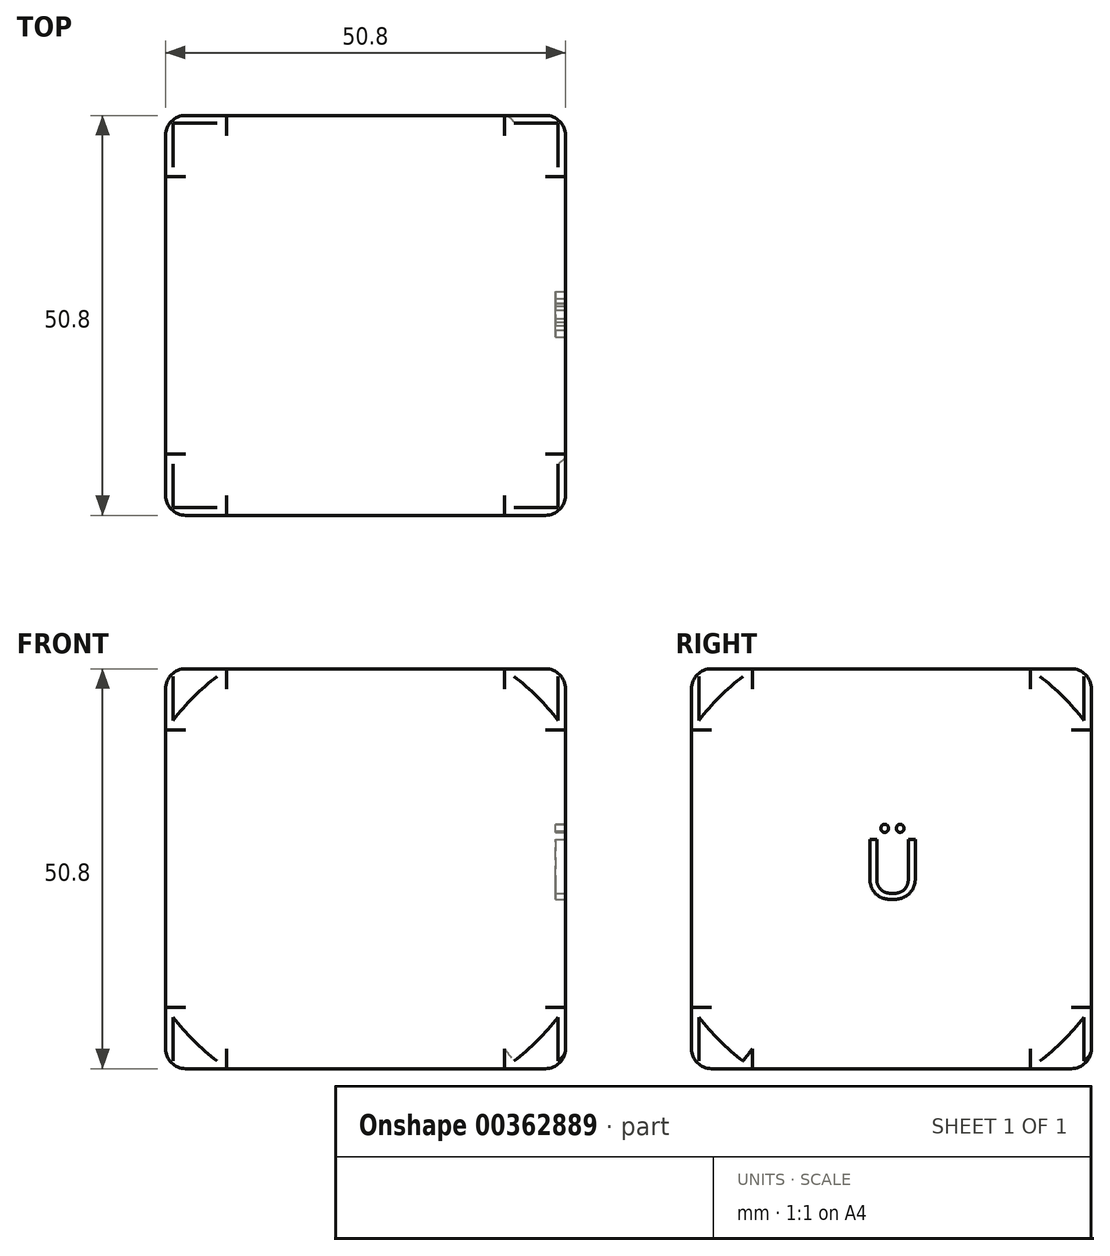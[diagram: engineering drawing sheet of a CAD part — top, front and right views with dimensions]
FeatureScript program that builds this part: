
annotation { "Feature Type Name" : "Feature", "Feature Type Description" : "" }
export const myFeature = defineFeature(function(context is Context, id is Id, definition is map)
    precondition{}
    {
        {
            var Q0;
            Q0=qCreatedBy(makeId("Front.planeOp"),FACE);
            var sketch = newSketch(context, id + "F0", { "sketchPlane" : qUnion([Q0])});
            skLineSegment(sketch, "E0.bottom", {"start": v(25.4, -25.4) * mm, "end": v(-25.4, -25.4) * mm});
            skLineSegment(sketch, "E0.top", {"start": v(25.4, 25.4) * mm, "end": v(-25.4, 25.4) * mm});
            skLineSegment(sketch, "E0.left", {"start": v(25.4, -25.4) * mm, "end": v(25.4, 25.4) * mm});
            skLineSegment(sketch, "E0.right", {"start": v(-25.4, -25.4) * mm, "end": v(-25.4, 25.4) * mm});
            skPoint(sketch, "E0.middle", {"position": v(0, 0) * mm});
            skSolve(sketch);
        }
        {
            var Q0;
            Q0 = qSketchRegion(id + "F0", true);
            extrude(context, id + "F1", {"entities" : qUnion([Q0]), "endBound" : BoundingType.SYMMETRIC, "oppositeDirection" : true, "depth" : 50.8 * mm});
        }
        {
            var Q0;
            Q0=qCreatedBy(makeId("Right.planeOp"),FACE);
            var sketch = newSketch(context, id + "F2", { "sketchPlane" : qUnion([Q0])});
            skArc(sketch, "E1", {"start": v(0, 39.37) * mm, "mid": v(-39.37, 0) * mm, "end": v(0, -39.37) * mm});
            skLineSegment(sketch, "E2", {"start": v(0, -76.2) * mm, "end": v(0, -39.37) * mm});
            skArc(sketch, "E3", {"start": v(0, 76.2) * mm, "mid": v(-76.2, 0) * mm, "end": v(0, -76.2) * mm});
            skPoint(sketch, "E4.orphan", {"position": v(0, 68.2) * mm});
            skLineSegment(sketch, "E5.trimOffspring", {"start": v(0, 39.37) * mm, "end": v(0, 76.2) * mm});
            skSolve(sketch);
        }
        {
            var Q0;
            Q0 = qSketchRegion(id + "F2", true);
            var Q1;
            Q1=sQuery(id+"F2.wireOp",EDGE,"E5.trimOffspring");
            revolve(context, id + "F3", {"operationType" : NewBodyOperationType.REMOVE, "entities" : qUnion([Q0]), "axis" : qUnion([Q1]), "revolveType" : RevolveType.FULL, "oppositeDirection" : true});
        }
        {
            var Q0;
            Q0=makeQuery(id+"F1.opExtrude","SWEPT_FACE",FACE,{"disambiguationData":[OSD([sQuery(id+"F0.wireOp",EDGE,"E0.right")])]});
            var Q1;
            Q1=makeQuery(id+"F1.opExtrude","SWEPT_FACE",FACE,{"disambiguationData":[OSD([sQuery(id+"F0.wireOp",EDGE,"E0.top")])]});
            var Q2;
            Q2=makeQuery(id+"F1.opExtrude","CAP_FACE",FACE,{"disambiguationData":[OSD([sQuery(id+"F0.wireOp",EDGE,"E0.bottom"),sQuery(id+"F0.wireOp",EDGE,"E0.top"),sQuery(id+"F0.wireOp",EDGE,"E0.left"),sQuery(id+"F0.wireOp",EDGE,"E0.right")])],"isStart":true});
            var Q3;
            Q3=makeQuery(id+"F1.opExtrude","SWEPT_FACE",FACE,{"disambiguationData":[OSD([sQuery(id+"F0.wireOp",EDGE,"E0.left")])]});
            var Q4;
            Q4=makeQuery(id+"F1.opExtrude","SWEPT_FACE",FACE,{"disambiguationData":[OSD([sQuery(id+"F0.wireOp",EDGE,"E0.bottom")])]});
            var Q5;
            Q5=makeQuery(id+"F1.opExtrude","CAP_FACE",FACE,{"disambiguationData":[OSD([sQuery(id+"F0.wireOp",EDGE,"E0.bottom"),sQuery(id+"F0.wireOp",EDGE,"E0.top"),sQuery(id+"F0.wireOp",EDGE,"E0.left"),sQuery(id+"F0.wireOp",EDGE,"E0.right")])],"isStart":false});
            fillet(context, id + "F4", {"entities" : qUnion([Q0, Q1, Q2, Q3, Q4, Q5]), "radius" : 2.54 * mm, "tangentPropagation" : true, "allowEdgeOverflow" : false});
        }
        {
            var Q0;
            Q0=makeQuery(id+"F1.opExtrude","SWEPT_FACE",FACE,{"disambiguationData":[OSD([sQuery(id+"F0.wireOp",EDGE,"E0.left")])]});
            var sketch = newSketch(context, id + "F5", { "sketchPlane" : qUnion([Q0])});
            skText(sketch, "E6", { "text": "Ü", "fontName": "OpenSans-Regular.ttf"});
            skLineSegment(sketch, "E7", {"start": v(-3.71, 0) * mm, "end": v(-22.86, 0) * mm, "construction": true});
            skPoint(sketch, "E7.endSnap0", {"position": v(-22.86, 0) * mm});
            skLineSegment(sketch, "E8", {"start": v(0, 22.86) * mm, "end": v(0, 3.8) * mm, "construction": true});
            const initialGuessF5  = {"E6": [-0.00371, -0.00381, 1, 0, 0.00762]};
            skSetInitialGuess(sketch, initialGuessF5);
            skSolve(sketch);
        }
        {
            var Q0;
            Q0 = qSketchRegion(id + "F5", true);
            extrude(context, id + "F6", {"entities" : qUnion([Q0]), "operationType" : NewBodyOperationType.REMOVE, "oppositeDirection" : true, "depth" : 1.27 * mm});
        }
    });
